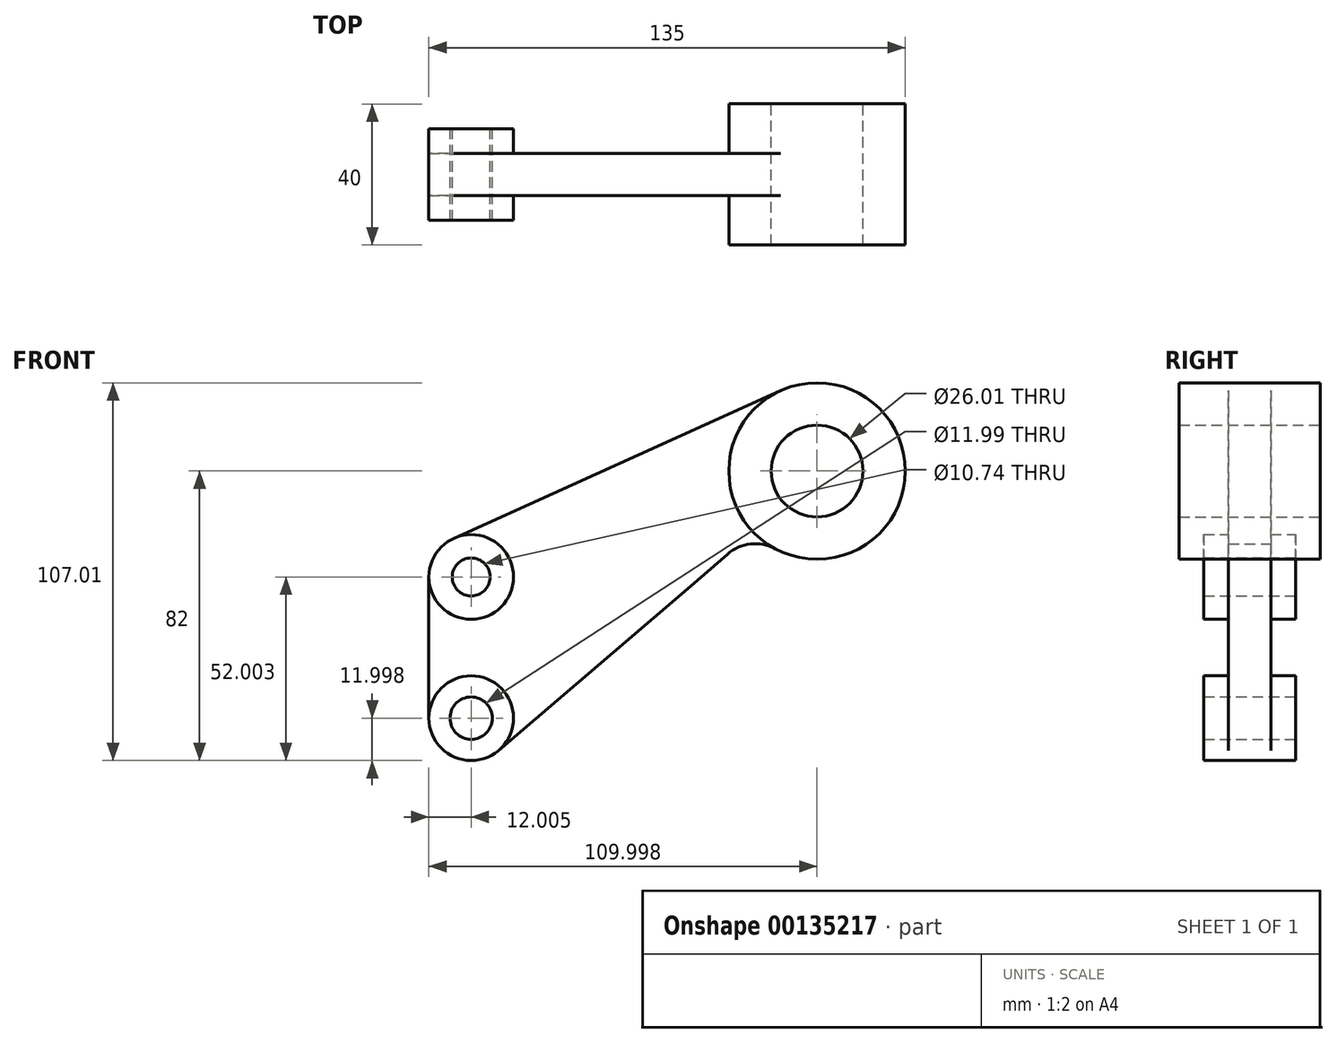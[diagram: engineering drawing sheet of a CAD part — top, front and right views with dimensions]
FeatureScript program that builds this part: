
annotation { "Feature Type Name" : "Feature", "Feature Type Description" : "" }
export const myFeature = defineFeature(function(context is Context, id is Id, definition is map)
    precondition{}
    {
        {
            var Q0;
            Q0=qCreatedBy(makeId("Front.planeOp"),FACE);
            var sketch = newSketch(context, id + "F0", { "sketchPlane" : qUnion([Q0])});
            skCircle(sketch, "E0", {"center": v(-60.52, -36.31) * mm, "radius": 6 * mm});
            skCircle(sketch, "E1", {"center": v(-60.52, -36.31) * mm, "radius": 12 * mm});
            skCircle(sketch, "E2", {"center": v(-60.52, 3.7) * mm, "radius": 5.37 * mm});
            skCircle(sketch, "E3", {"center": v(-60.52, 3.7) * mm, "radius": 12 * mm});
            skCircle(sketch, "E4", {"center": v(37.47, 33.69) * mm, "radius": 25 * mm});
            skLineSegment(sketch, "E5", {"start": v(-60.52, 3.7) * mm, "end": v(-60.52, -36.31) * mm, "construction": true});
            skLineSegment(sketch, "E6", {"start": v(-72.53, 3.7) * mm, "end": v(-72.53, -36.31) * mm});
            skCircle(sketch, "E7", {"center": v(37.47, 33.69) * mm, "radius": 13 * mm});
            skLineSegment(sketch, "E8", {"start": v(-65.47, 14.63) * mm, "end": v(27.17, 56.48) * mm});
            skLineSegment(sketch, "E9", {"start": v(-52.73, -45.43) * mm, "end": v(1.7, 1.1) * mm});
            skLineSegment(sketch, "E10", {"start": v(1.7, 1.1) * mm, "end": v(12.08, 10.14) * mm});
            skArc(sketch, "E11", {"start": v(12.08, 10.14) * mm, "mid": v(18.62, 13.02) * mm, "end": v(25.63, 11.66) * mm});
            skLineSegment(sketch, "E12", {"start": v(-60.52, -36.31) * mm, "end": v(-72.53, -36.31) * mm, "construction": true});
            skLineSegment(sketch, "E13", {"start": v(-60.52, 3.7) * mm, "end": v(-72.53, 3.7) * mm, "construction": true});
            skSolve(sketch);
        }
        {
            var Q0;
            {var subQ0=sQuery(id+"F0.wireOp",EDGE,"E6");Q0=makeQuery(id+"F0.imprint","IMPRINT",FACE,{"disambiguationData":[TD([[makeQuery(id+"F0.imprint","IMPRINT",EDGE,{"derivedFrom":subQ0}),1.0]])]});}
            extrude(context, id + "F1", {"entities" : qUnion([Q0]), "endBound" : BoundingType.SYMMETRIC, "depth" : 12 * mm});
        }
        {
            var Q0;
            Q0=makeQuery(id+"F0.imprint","IMPRINT",FACE,{"disambiguationData":[TD([[makeQuery(id+"F0.imprint","IMPRINT",EDGE,{"derivedFrom":sQuery(id+"F0.wireOp",EDGE,"E7")}),-1.0]])]});
            extrude(context, id + "F2", {"entities" : qUnion([Q0]), "operationType" : NewBodyOperationType.ADD, "endBound" : BoundingType.SYMMETRIC, "depth" : 40 * mm});
        }
        {
            var Q0;
            Q0=makeQuery(id+"F0.imprint","IMPRINT",FACE,{"disambiguationData":[TD([[makeQuery(id+"F0.imprint","IMPRINT",EDGE,{"derivedFrom":sQuery(id+"F0.wireOp",EDGE,"E2")}),-1.0]])]});
            var Q1;
            Q1=makeQuery(id+"F0.imprint","IMPRINT",FACE,{"disambiguationData":[TD([[makeQuery(id+"F0.imprint","IMPRINT",EDGE,{"derivedFrom":sQuery(id+"F0.wireOp",EDGE,"E0")}),-1.0]])]});
            extrude(context, id + "F3", {"entities" : qUnion([Q0, Q1]), "operationType" : NewBodyOperationType.ADD, "endBound" : BoundingType.SYMMETRIC, "depth" : 26 * mm});
        }
    });
